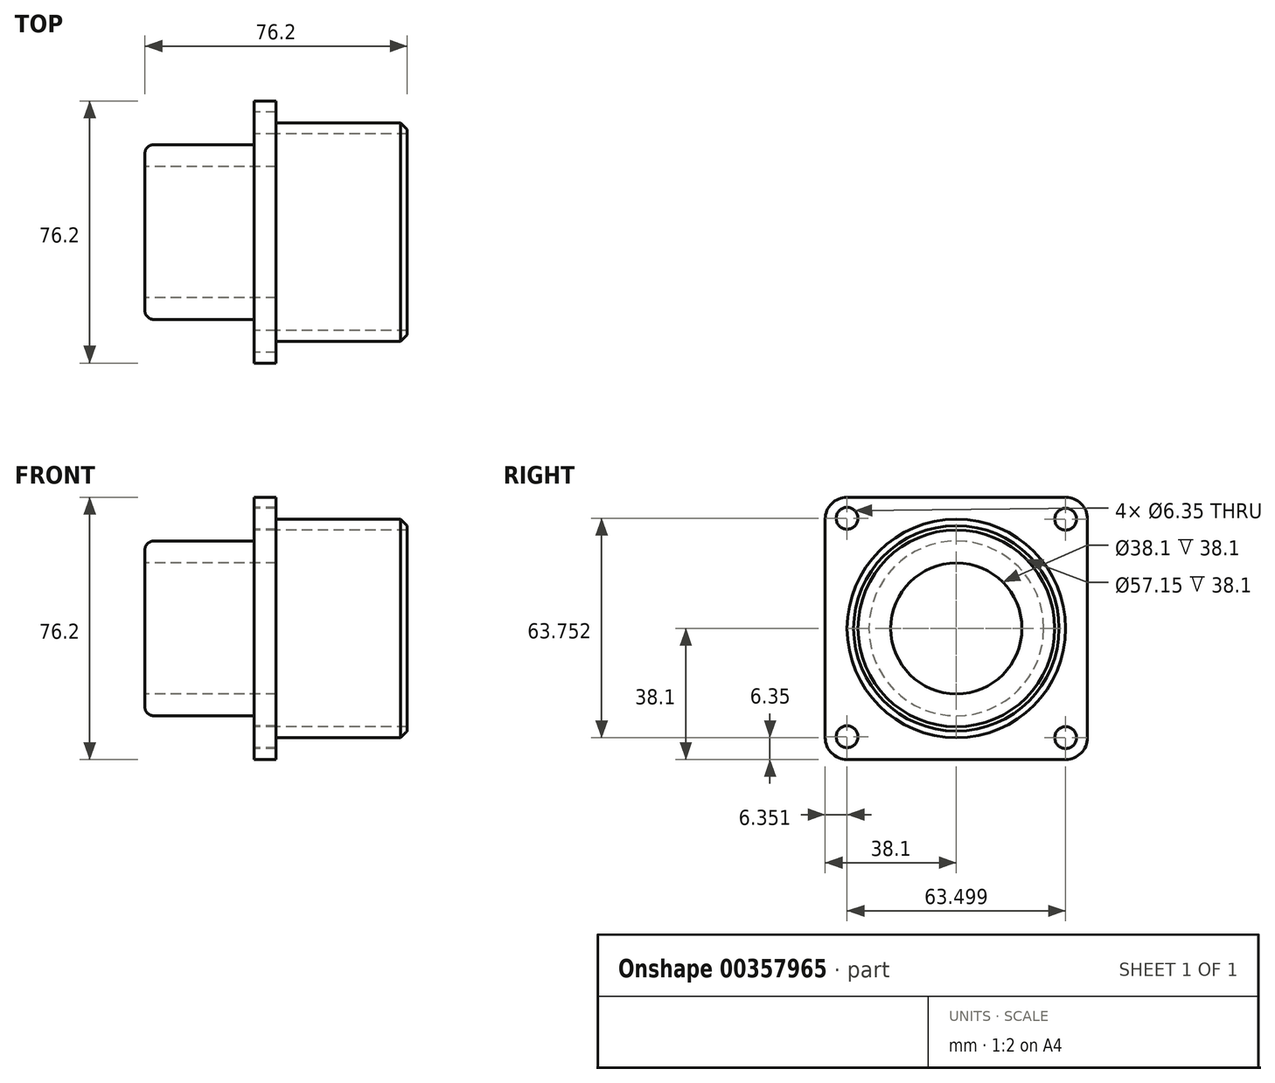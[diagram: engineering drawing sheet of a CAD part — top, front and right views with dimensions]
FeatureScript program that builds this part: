
annotation { "Feature Type Name" : "Feature", "Feature Type Description" : "" }
export const myFeature = defineFeature(function(context is Context, id is Id, definition is map)
    precondition{}
    {
        {
            var Q0;
            Q0=qCreatedBy(makeId("Right.planeOp"),FACE);
            var sketch = newSketch(context, id + "F0", { "sketchPlane" : qUnion([Q0])});
            skLineSegment(sketch, "E0.bottom", {"start": v(-31.75, -38.1) * mm, "end": v(31.75, -38.1) * mm});
            skLineSegment(sketch, "E0.top", {"start": v(-31.75, 38.1) * mm, "end": v(31.75, 38.1) * mm});
            skLineSegment(sketch, "E0.left", {"start": v(-38.1, -31.75) * mm, "end": v(-38.1, 31.75) * mm});
            skLineSegment(sketch, "E0.right", {"start": v(38.1, -31.75) * mm, "end": v(38.1, 31.75) * mm});
            skPoint(sketch, "E0.middle", {"position": v(0, 0) * mm});
            skPoint(sketch, "E1.visualSharp", {"position": v(-38.1, 38.1) * mm});
            skArc(sketch, "E1.filletArc", {"start": v(-31.75, 38.1) * mm, "mid": v(-36.24, 36.24) * mm, "end": v(-38.1, 31.75) * mm});
            skPoint(sketch, "E2.visualSharp", {"position": v(38.1, 38.1) * mm});
            skArc(sketch, "E2.filletArc", {"start": v(38.1, 31.75) * mm, "mid": v(36.24, 36.24) * mm, "end": v(31.75, 38.1) * mm});
            skPoint(sketch, "E3.visualSharp", {"position": v(38.1, -38.1) * mm});
            skArc(sketch, "E3.filletArc", {"start": v(31.75, -38.1) * mm, "mid": v(36.24, -36.24) * mm, "end": v(38.1, -31.75) * mm});
            skPoint(sketch, "E4.visualSharp", {"position": v(-38.1, -38.1) * mm});
            skArc(sketch, "E4.filletArc", {"start": v(-38.1, -31.75) * mm, "mid": v(-36.24, -36.24) * mm, "end": v(-31.75, -38.1) * mm});
            skCircle(sketch, "E5", {"center": v(0, 0) * mm, "radius": 19.05 * mm});
            skCircle(sketch, "E6", {"center": v(31.75, 31.75) * mm, "radius": 3.18 * mm});
            skCircle(sketch, "E7.0.1.0", {"center": v(31.75, -31.75) * mm, "radius": 3.18 * mm});
            skCircle(sketch, "E7.1.0.0", {"center": v(-31.75, 32) * mm, "radius": 3.18 * mm});
            skCircle(sketch, "E7.1.1.0", {"center": v(-31.75, -31.5) * mm, "radius": 3.18 * mm});
            skLineSegment(sketch, "E7.direction1", {"start": v(31.75, 31.75) * mm, "end": v(-31.75, 32) * mm, "construction": true});
            skLineSegment(sketch, "E7.direction2", {"start": v(31.75, 31.75) * mm, "end": v(31.75, -31.75) * mm, "construction": true});
            skSolve(sketch);
        }
        {
            var Q0;
            Q0=makeQuery(id+"F0.imprint","IMPRINT",FACE,{"disambiguationData":[TD([[makeQuery(id+"F0.imprint","IMPRINT",EDGE,{"derivedFrom":sQuery(id+"F0.wireOp",EDGE,"E0.bottom")}),1.0]])]});
            extrude(context, id + "F1", {"entities" : qUnion([Q0]), "depth" : 6.35 * mm});
        }
        {
            var Q0;
            Q0=qCreatedBy(makeId("Right.planeOp"),FACE);
            var sketch = newSketch(context, id + "F2", { "sketchPlane" : qUnion([Q0])});
            skCircle(sketch, "E8", {"center": v(0, 0) * mm, "radius": 31.75 * mm});
            skCircle(sketch, "E9", {"center": v(0, 0) * mm, "radius": 28.58 * mm});
            skSolve(sketch);
        }
        {
            var Q0;
            Q0 = qSketchRegion(id + "F2", true);
            extrude(context, id + "F3", {"entities" : qUnion([Q0]), "operationType" : NewBodyOperationType.ADD, "depth" : 44.45 * mm});
        }
        {
            var Q0;
            Q0=makeQuery(id+"F3.opExtrude","CAP_EDGE",EDGE,{"disambiguationData":[OSD([sQuery(id+"F2.wireOp",EDGE,"E8")])],"isStart":false});
            chamfer(context, id + "F4", {"entities" : qUnion([Q0]), "chamferType" : ChamferType.OFFSET_ANGLE, "width" : 1.9 * mm, "oppositeDirection" : false, "angle" : 45 * degree, "tangentPropagation" : true});
        }
        {
            var Q0;
            Q0=qCreatedBy(makeId("Right.planeOp"),FACE);
            var sketch = newSketch(context, id + "F5", { "sketchPlane" : qUnion([Q0])});
            skCircle(sketch, "E10", {"center": v(0, 0) * mm, "radius": 19.05 * mm});
            skCircle(sketch, "E11", {"center": v(0, 0) * mm, "radius": 25.4 * mm});
            skSolve(sketch);
        }
        {
            var Q0;
            Q0 = qSketchRegion(id + "F5", true);
            extrude(context, id + "F6", {"entities" : qUnion([Q0]), "operationType" : NewBodyOperationType.ADD, "oppositeDirection" : true, "depth" : 31.75 * mm});
        }
        {
            var Q0;
            Q0=makeQuery(id+"F6.opExtrude","CAP_EDGE",EDGE,{"disambiguationData":[OSD([sQuery(id+"F5.wireOp",EDGE,"E11")])],"isStart":false});
            fillet(context, id + "F7", {"entities" : qUnion([Q0]), "radius" : 2.54 * mm, "tangentPropagation" : true, "allowEdgeOverflow" : false});
        }
    });
